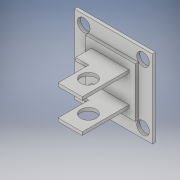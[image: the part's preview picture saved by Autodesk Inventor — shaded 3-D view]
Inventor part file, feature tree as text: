
AUTODESK INVENTOR PART (.ipt)
format: ipt  version: 2018 (Build 220112000, 112)  size: 177,664 bytes
history: native  units: in
note: dims shown in document units (in); Inventor stores cm internally (conversion verified against a paired STEP export)
features: extrude x6, sketch x5
ambient origin geometry x8: Origin, YZ Plane, XZ Plane, XY Plane, X Axis, Y Axis, Z Axis, Center Point
bodies: Solid1 (feature_tree)
feature tree (11):
  extrude  "Extrusion1"  Depth=1.25in
  extrude  "Extrusion2"  Depth=0.225in
  extrude  "Extrusion3"  Depth=0.225in
  extrude  "Extrusion4"  Depth=0.05in TaperAngle=0.0deg
  extrude  "Extrusion5"  Depth=0.05in
  extrude  "Extrusion6"  Depth=0.05in
  sketch  "Sketch1"  dims[d0=1.25in d1=1.25in]
  sketch  "Sketch2"  dims[d2=0.05in d3=0.0in d4=0.225in]
  sketch  "Sketch4"  dims[d5=0.225in d6=0.225in]
  sketch  "Sketch5"  dims[d7=0.225in d8=0.05in d9=0.0in]
  sketch  "Sketch6"  dims[d18=0.75in d19=0.0in d20=0.25in d21=0.3in d22=5.0in d23=0.0in d24=0.2031in d28=0.2031in d29=0.15in d30=0.15in d31=0.15in d32=0.15in d33=0.2031in d34=0.15in d35=0.15in d36=0.2031in d37=0.15in d38=0.15in d42=0.5in d43=0.0in d44=0.4in d45=4.0in d46=0.0in d48=0.05in d49=0.437in d50=0.05in d60=0.05in d61=0.2185in]
